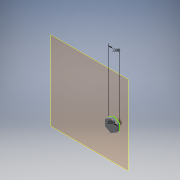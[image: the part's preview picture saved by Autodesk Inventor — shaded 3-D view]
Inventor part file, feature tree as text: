
AUTODESK INVENTOR PART (.ipt)
format: ipt  version: 2016 (Build 200138000, 138)  size: 101,888 bytes
history: native  units: in
note: dims shown in document units (in); Inventor stores cm internally (conversion verified against a paired STEP export)
features: extrude x2, plane x1, sketch x1
ambient origin geometry x8: Origin, YZ Plane, XZ Plane, XY Plane, X Axis, Y Axis, Z Axis, Center Point
bodies: Solid1 (feature_tree)
feature tree (4):
  plane  "Work Plane1"
  sketch  "Sketch1"  dims[d0=0.0984in d1=0.0591in d2=0.0394in d3=0.0in d6=0.0295in d7=0.0in]
  extrude  "Extrusion1"  Depth=0.0295in
  extrude  "Extrusion3"  Depth=0.0394in TaperAngle=0.0deg
